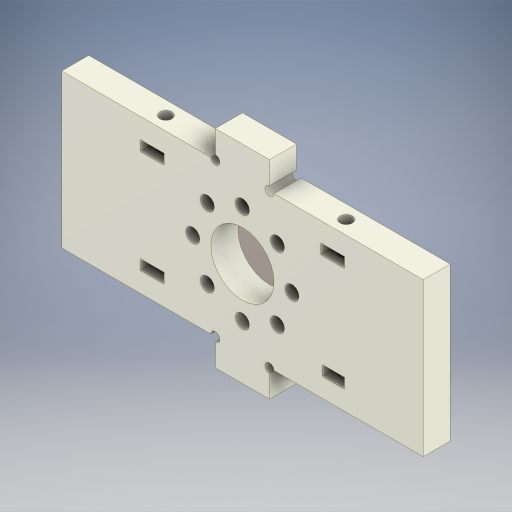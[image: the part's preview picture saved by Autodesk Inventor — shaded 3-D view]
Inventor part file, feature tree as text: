
AUTODESK INVENTOR PART (.ipt)
format: ipt  version: 2024 (Build 280153000, 153)  size: 375,808 bytes
history: native  units: in
note: dims shown in document units (in); Inventor stores cm internally (conversion verified against a paired STEP export)
features: other x4, extrude x4, sketch x4, reference x1, projected_geometry x1
ambient origin geometry x8: Origin, YZ Plane, XZ Plane, XY Plane, X Axis, Y Axis, Z Axis, Center Point
bodies: Body1 (feature_tree)
feature tree (14):
  other  "솔리드1"
  other  "작업 평면1"
  extrude  "돌출1"  Depth=3.1575in
  extrude  "돌출2"  Depth=1.3386in
  extrude  "돌출4"  Depth=0.0787in
  extrude  "돌출5"  Depth=0.1063in
  sketch  "스케치1"
  reference  "참조1"
  sketch  "스케치3"
  sketch  "스케치4"
  sketch  "스케치5"
  projected_geometry  "투영된 루프1"
  other  "조립품14"
  other  "64-106Horn:1"
